# Revit family: Trane_TVR_Outdoor_4TVH0115E8000AA_20200410_V1
name_source: partatom
category: Equipamento mecânico
units: mm (PartAtom-declared; Revit-internal decimal feet)

## family parameters
Com base no plano de trabalho = Não
Compartilhado = Não
Corte com vazios quando carregada = Não
Cota do conector redondo = Utilizar diâmetro
Número OmniClass = 23.75.00.00
Ponto de cálculo do ambiente = Não
Sempre na vertical = Sim
Tipo de parte = Normal
Título OmniClass = Climate Control (HVAC)

## types (1)
- 4TVH0115E8000AA
    Air Flow = 11000.000 m³/h
    Casing color = White
    Compressor = 1
    Condensation = Air
    Cooling Capacity = 33.500 kW
    Cooling Power Input = 7.080 kW
    Depth = 790  [stored 2.59186 ft]
    Descrição = High efficiency air cooled
    Fabricante = Trane
    Gas = R410A
    Gas pipe = 28.6
    Heating Capacity = 33.500 kW
    Heating Power Input = 6.650 kW
    Height = 1635  [stored 5.36417 ft]
    Installation = Outdoor installation
    Liquid pipe = 15.9  [stored 0.0521654 ft]
    Machine material = Galvanized Steel
    Maximum Fuse Amps = 50 A
    Minimum Circuit Amps = 39 A
    Modelo = 4TVH0115E8000AA
    Net Weight = 227.00 kg
    Power supply = 220V 3Ph~60Hz
    Series = ULTRA
    URL = https://www.trane.com
    Width = 990  [stored 3.24803 ft]
    clearance access behind = 1000  [stored 3.28084 ft]
    clearance access front = 1000  [stored 3.28084 ft]
    clearance access left = 1000  [stored 3.28084 ft]
    clearance access right = 1000  [stored 3.28084 ft]

note: [stored X ft] marks values corroborated as IEEE doubles in the binary element streams (Revit-internal decimal feet)

## geometry (parser evidence)
native form markers: Sweep x24
no freeform markers — native parametric forms only
